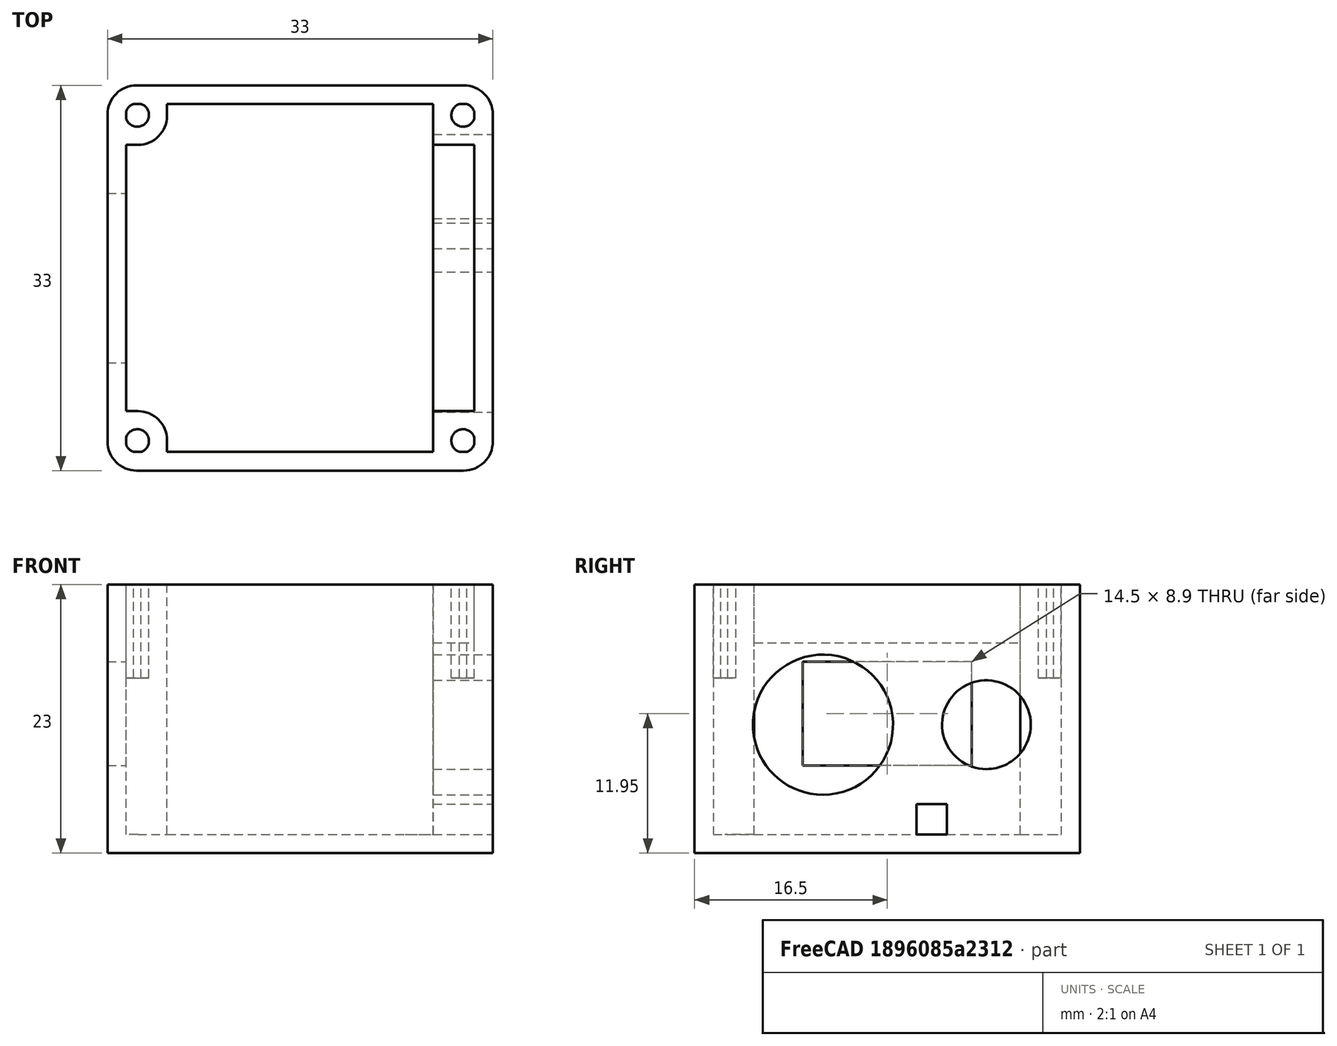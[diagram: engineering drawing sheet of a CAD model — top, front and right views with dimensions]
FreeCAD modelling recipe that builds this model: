
FCSTD DOCUMENT  (FreeCAD 0.16R)
Label: SolderungIron_Tiny13
License: All rights reserved
LicenseURL: http://en.wikipedia.org/wiki/All_rights_reserved
objects: Part::Box×9, Part::Cut×7, Part::Cylinder×6, Part::MultiFuse×4, Part::Fillet×1
note: 27 computed .brp shape members not serialized (recipe doc carries the construction recipe); baked Part::Feature solids carry a one-line shape summary decoded from their .brp

FEATURE [Part::Box] Box  label="Aussen"
  Height = 23
  Length = 33
  Width = 33
FEATURE [Part::Box] Box001  label="Innen"
  Height = 23
  Length = 29.8
  Placement = pos=(1.6,1.6,1.6) rot=(0,0,1;0rad)
  Width = 29.8
FEATURE [Part::Cut] Cut  label="Rohgehaeuse"
  Base = -> Box
  Placement = pos=(25.5,0,0) rot=(0,0,1;0rad)
  Tool = -> Box001
FEATURE [Part::Box] Box002  label="Schraubhalter"
  Height = 23
  Length = 5.1
  Width = 5.1
FEATURE [Part::Cylinder] Cylinder  label="Schraubloch"
  Angle = 360
  Height = 8
  Placement = pos=(2.55,2.55,15) rot=(0,0,1;0rad)
  Radius = 1
FEATURE [Part::Cut] Cut001  label="Platinenhalter000"
  Base = -> Box002
  Placement = pos=(25.5,0,0) rot=(0,0,1;0rad)
  Tool = -> Cylinder
FEATURE [Part::Box] Box003  label="Schraubhalter001"
  Height = 23
  Length = 5.1
  Width = 5.1
FEATURE [Part::Cylinder] Cylinder001  label="Schraubloch001"
  Angle = 360
  Height = 8
  Placement = pos=(2.55,2.55,15) rot=(0,0,1;0rad)
  Radius = 1
FEATURE [Part::Cut] Cut002  label="Platinenhalter001"
  Base = -> Box003
  Placement = pos=(53.4,0,0) rot=(0,0,1;0rad)
  Tool = -> Cylinder001
FEATURE [Part::Box] Box004  label="Schraubhalter002"
  Height = 23
  Length = 5.1
  Width = 5.1
FEATURE [Part::Cylinder] Cylinder002  label="Schraubloch002"
  Angle = 360
  Height = 8
  Placement = pos=(2.55,2.55,15) rot=(0,0,1;0rad)
  Radius = 1
FEATURE [Part::Cut] Cut003  label="Platinenhalter002"
  Base = -> Box004
  Placement = pos=(25.5,27.9,0) rot=(0,0,1;0rad)
  Tool = -> Cylinder002
FEATURE [Part::Box] Box005  label="Schraubhalter003"
  Height = 23
  Length = 5.1
  Width = 5.1
FEATURE [Part::Cylinder] Cylinder003  label="Schraubloch003"
  Angle = 360
  Height = 8
  Placement = pos=(2.55,2.55,15) rot=(0,0,1;0rad)
  Radius = 1
FEATURE [Part::Cut] Cut004  label="Platinenhalter003"
  Base = -> Box005
  Placement = pos=(53.4,27.9,0) rot=(0,0,1;0rad)
  Tool = -> Cylinder003
FEATURE [Part::MultiFuse] Fusion  label="Platinenhalter"
  Shapes = -> [Cut001,Cut002,Cut004,Cut003]
FEATURE [Part::MultiFuse] Fusion001  label="Grundgehaeuse"
  Shapes = -> [Cut,Fusion]
FEATURE [Part::Box] Box006  label="Switch"
  Height = 8.9
  Length = 10
  Placement = pos=(22.5,9.25,7.5) rot=(0,0,1;0rad)
  Width = 14.5
FEATURE [Part::Cylinder] Cylinder004  label="Aviator"
  Angle = 360
  Height = 10
  Placement = pos=(50,11,11) rot=(0,1,0;1.5708rad)
  Radius = 6
FEATURE [Part::Cylinder] Cylinder005  label="DCPlug"
  Angle = 360
  Height = 10
  Placement = pos=(50,25,11) rot=(0,1,0;1.5708rad)
  Radius = 3.8
FEATURE [Part::Box] Box007  label="Lochverstaerkung"
  Height = 18
  Length = 5.1
  Placement = pos=(53.4,5.1,0) rot=(0,0,1;0rad)
  Width = 22.8
FEATURE [Part::MultiFuse] Fusion002  label="Gehaeusex"
  Shapes = -> [Fusion001,Box007]
FEATURE [Part::MultiFuse] Fusion003  label="Aussparungen"
  Shapes = -> [Box006,Cylinder004,Cylinder005]
FEATURE [Part::Fillet] Fillet  label="Gehaeusez"
  Base = -> Fusion002
  Edges = 6 edges r=2.5: [Edge1,Edge43,Edge45,Edge68,Edge95,Edge110]
FEATURE [Part::Cut] Cut005  label="Case_old"
  Base = -> Fillet
  Tool = -> Fusion003
FEATURE [Part::Box] Box008  label="Dupont"
  Height = 2.6
  Length = 10
  Placement = pos=(51,19,1.6) rot=(0,0,1;0rad)
  Width = 2.6
FEATURE [Part::Cut] Cut006  label="Case"
  Base = -> Cut005
  Tool = -> Box008
